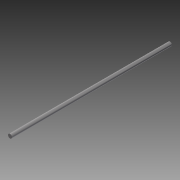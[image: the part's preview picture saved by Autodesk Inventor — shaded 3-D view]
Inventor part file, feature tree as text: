
AUTODESK INVENTOR PART (.ipt)
format: ipt  version: 2014 SP1 (Build 180222100, 222)  size: 81,408 bytes
history: native  units: mm
features: extrude x1, sketch x1
ambient origin geometry x8: Origin, YZ Plane, XZ Plane, XY Plane, X Axis, Y Axis, Z Axis, Center Point
bodies: Solid1 (feature_tree)
feature tree (2):
  extrude  "Extrusion1"  Depth=380.0mm TaperAngle=0.0deg
  sketch  "Sketch1"  dims[d0=9.525mm d1=380.0mm d2=0.0mm]
